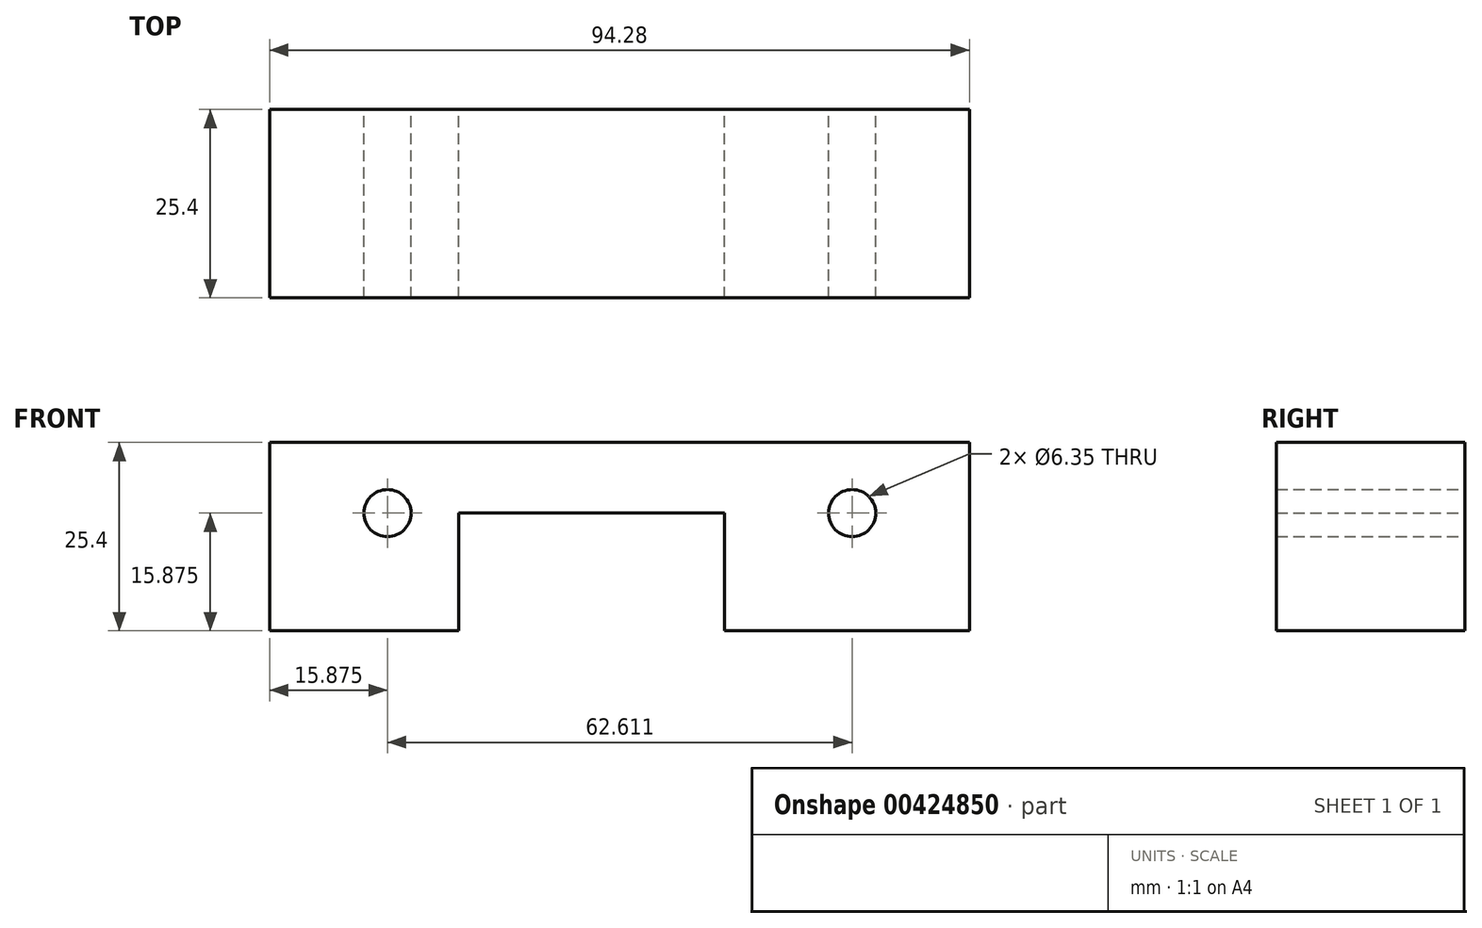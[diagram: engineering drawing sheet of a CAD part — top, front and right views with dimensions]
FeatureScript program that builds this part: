
annotation { "Feature Type Name" : "Feature", "Feature Type Description" : "" }
export const myFeature = defineFeature(function(context is Context, id is Id, definition is map)
    precondition{}
    {
        {
            var Q0;
            Q0=qCreatedBy(makeId("Front.planeOp"),FACE);
            var sketch = newSketch(context, id + "F0", { "sketchPlane" : qUnion([Q0])});
            skLineSegment(sketch, "E0", {"start": v(0, 0) * mm, "end": v(94.28, 0) * mm});
            skLineSegment(sketch, "E1", {"start": v(94.28, 0) * mm, "end": v(94.28, -25.4) * mm});
            skLineSegment(sketch, "E2", {"start": v(94.28, -25.4) * mm, "end": v(61.26, -25.4) * mm});
            skLineSegment(sketch, "E3", {"start": v(61.26, -25.4) * mm, "end": v(61.26, -9.53) * mm});
            skLineSegment(sketch, "E4", {"start": v(61.26, -9.53) * mm, "end": v(25.45, -9.53) * mm});
            skLineSegment(sketch, "E5", {"start": v(25.45, -9.53) * mm, "end": v(25.45, -25.4) * mm});
            skLineSegment(sketch, "E6", {"start": v(27.68, -25.4) * mm, "end": v(0, -25.4) * mm});
            skLineSegment(sketch, "E7", {"start": v(0, -25.4) * mm, "end": v(0, 0) * mm});
            skCircle(sketch, "E8", {"center": v(15.88, -9.53) * mm, "radius": 3.18 * mm});
            skCircle(sketch, "E9", {"center": v(78.49, -9.53) * mm, "radius": 3.18 * mm});
            skSolve(sketch);
        }
        {
            var Q0;
            Q0 = qSketchRegion(id + "F0", true);
            extrude(context, id + "F1", {"entities" : qUnion([Q0]), "depth" : 25.4 * mm});
        }
    });
